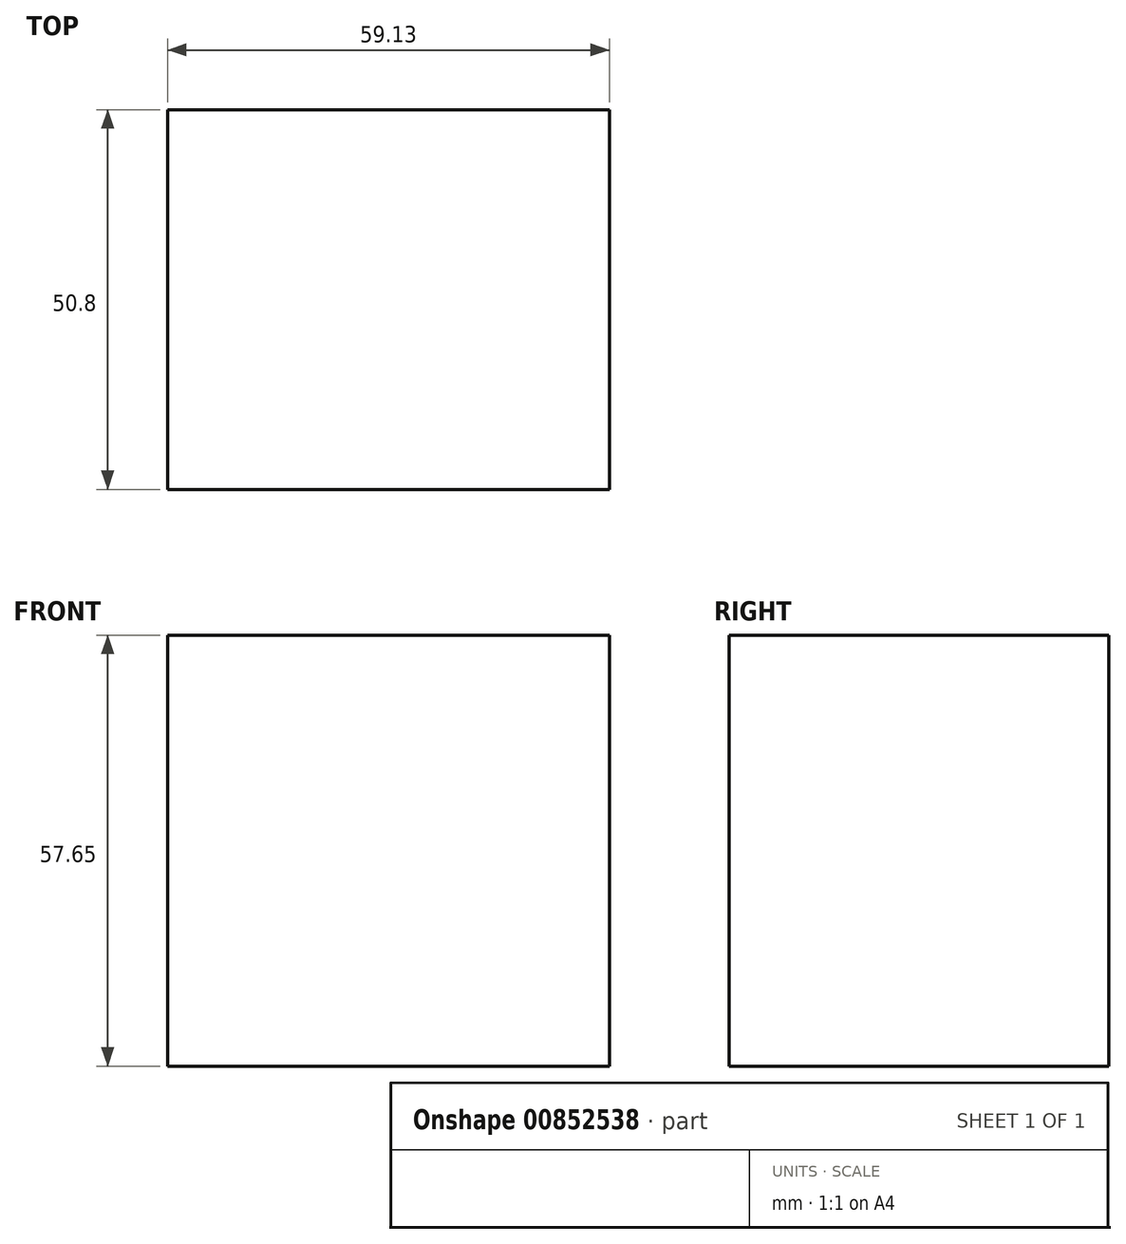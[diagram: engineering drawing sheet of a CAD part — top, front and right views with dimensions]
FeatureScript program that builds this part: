
annotation { "Feature Type Name" : "Feature", "Feature Type Description" : "" }
export const myFeature = defineFeature(function(context is Context, id is Id, definition is map)
    precondition{}
    {
        {
            var Q0;
            Q0=qCreatedBy(makeId("Front.planeOp"),FACE);
            var sketch = newSketch(context, id + "F0", { "sketchPlane" : qUnion([Q0])});
            skLineSegment(sketch, "E0", {"start": v(0, 0) * mm, "end": v(59.13, 0) * mm});
            skLineSegment(sketch, "E1", {"start": v(59.13, 0) * mm, "end": v(59.13, 57.65) * mm});
            skLineSegment(sketch, "E2", {"start": v(59.13, 57.65) * mm, "end": v(0, 57.65) * mm});
            skLineSegment(sketch, "E3", {"start": v(0, 57.65) * mm, "end": v(0, 0) * mm});
            skSolve(sketch);
        }
        {
            var Q0;
            Q0=makeQuery(id+"F0.imprint","IMPRINT",FACE,{"disambiguationData":[TD([[makeQuery(id+"F0.imprint","IMPRINT",EDGE,{"derivedFrom":sQuery(id+"F0.wireOp",EDGE,"E0")}),1.0]])]});
            extrude(context, id + "F1", {"entities" : qUnion([Q0]), "depth" : 50.8 * mm, "offsetDistance" : 25.4 * mm});
        }
    });
